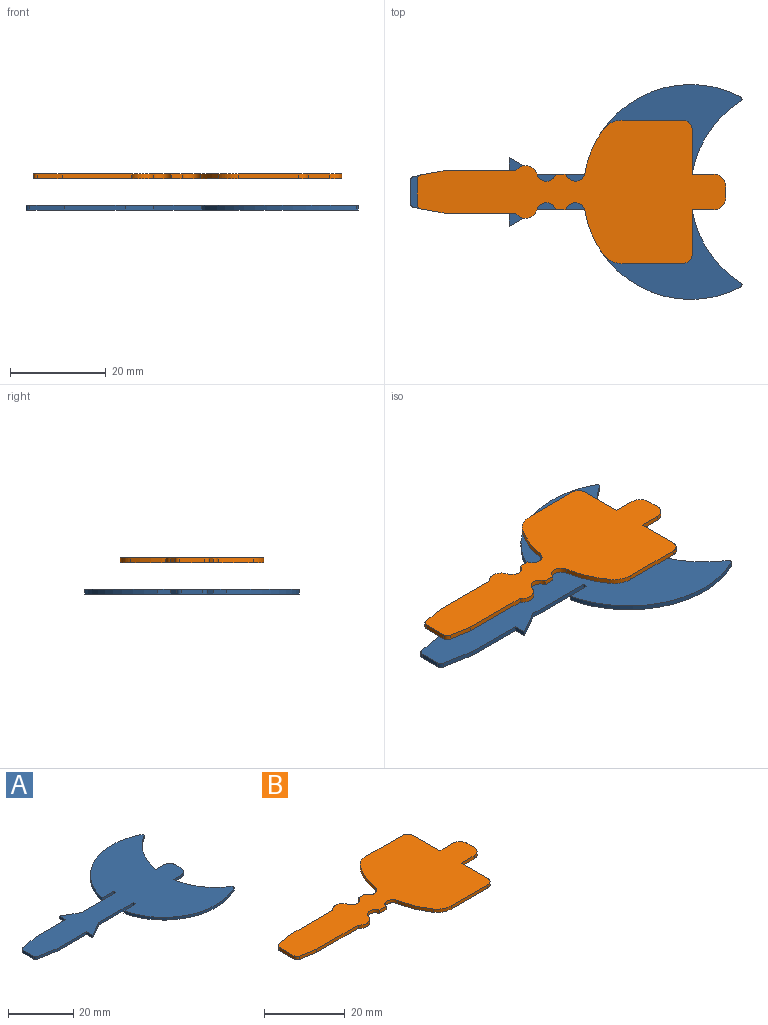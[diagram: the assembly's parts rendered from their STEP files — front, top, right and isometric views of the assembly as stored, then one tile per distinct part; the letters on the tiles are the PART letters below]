
ASSEMBLY  parts=2 mates=1
PART A: 30 faces, bbox 69.5x45x1 mm
  f0: plane 2.5x1mm, normal (1,0,0), area 2.5mm2, adj f12,f13,f14,f27
  f1: plane 3.5x1mm, normal (0,1,0), area 3.5mm2, adj f2,f12,f13,f14
  f2: cylinder r=22.5mm len=15.29mm, axis (0,0,-1), area 18.9mm2, adj f1,f12,f13,f15
  f3: cylinder r=22.5mm len=32.48mm, axis (0,0,-1), area 41.5mm2, adj f4,f12,f13,f15
  f4: plane 5x1mm, normal (0,-1,0), area 5mm2, adj f3,f5,f12,f13
  f5: plane 1x1mm, normal (-1,0,0), area 1mm2, adj f4,f6,f12,f13
  f6: plane 15x1mm, normal (0,1,0), area 15mm2, adj f5,f7,f12,f13
  f7: plane 6x3.46mm, normal (0.5,0.87,0), area 6.9mm2, adj f6,f8,f12,f13
  f8: plane 2.71x1mm, normal (-1,0,0), area 2.7mm2, adj f7,f9,f12,f13
  f9: plane 12.76x1mm, normal (0,1,0), area 12.8mm2, adj f8,f10,f12,f13
  f10: plane 7.17x1.27mm, normal (-0.17,0.98,0), area 7.3mm2, adj f9,f12,f13,f16
  f11: plane 4.5x1mm, normal (-1,0,0), area 4.5mm2, adj f12,f13,f16,f29
  f12: plane 69.5x45mm, normal (0,0,1), area 1314.9mm2, adj f0,f1,f2,f3,f4,f5,f6,f7
  f13: plane 69.5x45mm, normal (0,0,-1), area 1314.9mm2, adj f0,f1,f2,f3,f4,f5,f6,f7
  f14: cylinder r=2.5mm len=2.5mm, axis (0,0,1), area 3.9mm2, adj f0,f1,f12,f13
  f15: cylinder r=0.5mm len=1mm, axis (0,0,1), area 1mm2, adj f2,f3,f12,f13
  f16: cylinder r=1mm len=1mm, axis (0,0,-1), area 1.4mm2, adj f10,f11,f12,f13
  f17: plane 3.5x1mm, normal (0,-1,0), area 3.5mm2, adj f12,f13,f18,f27
  f18: cylinder r=22.5mm len=15.29mm, axis (0,0,-1), area 18.9mm2, adj f12,f13,f17,f28
  f19: cylinder r=22.5mm len=32.48mm, axis (0,0,-1), area 41.5mm2, adj f12,f13,f20,f28
  f20: plane 5x1mm, normal (0,1,0), area 5mm2, adj f12,f13,f19,f21
  f21: plane 1x1mm, normal (-1,0,0), area 1mm2, adj f12,f13,f20,f22
  f22: plane 15x1mm, normal (0,-1,0), area 15mm2, adj f12,f13,f21,f23
  f23: plane 6x3.46mm, normal (0.5,-0.87,0), area 6.9mm2, adj f12,f13,f22,f24
  f24: plane 2.71x1mm, normal (-1,0,0), area 2.7mm2, adj f12,f13,f23,f25
  f25: plane 12.76x1mm, normal (0,-1,0), area 12.8mm2, adj f12,f13,f24,f26
  f26: plane 7.17x1.27mm, normal (-0.17,-0.98,0), area 7.3mm2, adj f12,f13,f25,f29
  f27: cylinder r=2.5mm len=2.5mm, axis (0,0,1), area 3.9mm2, adj f0,f12,f13,f17
  f28: cylinder r=0.5mm len=1mm, axis (0,0,1), area 1mm2, adj f12,f13,f18,f19
  f29: cylinder r=1mm len=1mm, axis (0,0,-1), area 1.4mm2, adj f11,f12,f13,f26
PART B: 32 faces, bbox 64.5x30x1 mm
  f0: plane 2.5x1mm, normal (1,0,0), area 2.5mm2, adj f10,f11,f12,f26
  f1: plane 4.5x1mm, normal (0,1,0), area 4.5mm2, adj f10,f11,f12,f15
  f2: cylinder r=22.5mm len=8.95mm, axis (0,0,-1), area 9.8mm2, adj f3,f10,f11,f16
  f3: cylinder r=2mm len=3.91mm, axis (0,0,-1), area 5.4mm2, adj f2,f4,f10,f11
  f4: plane 2.24x1mm, normal (0,1,0), area 2.2mm2, adj f3,f5,f10,f11
  f5: cylinder r=2mm len=3.86mm, axis (0,0,-1), area 5.2mm2, adj f4,f6,f10,f11
  f6: cylinder r=2.5mm len=4.4mm, axis (0,0,-1), area 5.5mm2, adj f5,f7,f10,f11
  f7: plane 14.63x1mm, normal (0,1,0), area 14.6mm2, adj f6,f8,f10,f11
  f8: plane 5.17x1mm, normal (-0.17,0.98,0), area 5.3mm2, adj f7,f10,f11,f13
  f9: plane 5.21x1mm, normal (-1,0,0), area 5.2mm2, adj f10,f11,f13,f27
  f10: plane 64.5x30mm, normal (0,0,1), area 956.7mm2, adj f0,f1,f2,f3,f4,f5,f6,f7
  f11: plane 64.5x30mm, normal (0,0,-1), area 956.7mm2, adj f0,f1,f2,f3,f4,f5,f6,f7
  f12: cylinder r=2.5mm len=2.5mm, axis (0,0,1), area 3.9mm2, adj f0,f1,f10,f11
  f13: cylinder r=1mm len=1mm, axis (0,0,-1), area 1.4mm2, adj f8,f9,f10,f11
  f14: plane 12.68x1mm, normal (0,1,0), area 12.7mm2, adj f10,f11,f16,f17
  f15: plane 9.25x1mm, normal (1,0,0), area 9.2mm2, adj f1,f10,f11,f17
  f16: cylinder r=5mm len=4.1mm, axis (0,0,-1), area 4.8mm2, adj f2,f10,f11,f14
  f17: cylinder r=2mm len=2mm, axis (0,0,-1), area 3.1mm2, adj f10,f11,f14,f15
  f18: plane 4.5x1mm, normal (0,-1,0), area 4.5mm2, adj f10,f11,f26,f29
  f19: cylinder r=22.5mm len=8.95mm, axis (0,0,-1), area 9.8mm2, adj f10,f11,f20,f30
  f20: cylinder r=2mm len=3.91mm, axis (0,0,-1), area 5.4mm2, adj f10,f11,f19,f21
  f21: plane 2.24x1mm, normal (0,-1,0), area 2.2mm2, adj f10,f11,f20,f22
  f22: cylinder r=2mm len=3.86mm, axis (0,0,-1), area 5.2mm2, adj f10,f11,f21,f23
  f23: cylinder r=2.5mm len=4.4mm, axis (0,0,-1), area 5.5mm2, adj f10,f11,f22,f24
  f24: plane 14.63x1mm, normal (0,-1,0), area 14.6mm2, adj f10,f11,f23,f25
  f25: plane 5.17x1mm, normal (-0.17,-0.98,0), area 5.3mm2, adj f10,f11,f24,f27
  f26: cylinder r=2.5mm len=2.5mm, axis (0,0,1), area 3.9mm2, adj f0,f10,f11,f18
  f27: cylinder r=1mm len=1mm, axis (0,0,-1), area 1.4mm2, adj f9,f10,f11,f25
  f28: plane 12.68x1mm, normal (0,-1,0), area 12.7mm2, adj f10,f11,f30,f31
  f29: plane 9.25x1mm, normal (1,0,0), area 9.2mm2, adj f10,f11,f18,f31
  f30: cylinder r=5mm len=4.1mm, axis (0,0,-1), area 4.8mm2, adj f10,f11,f19,f28
  f31: cylinder r=2mm len=2mm, axis (0,0,-1), area 3.1mm2, adj f10,f11,f28,f29
PLACE A t=(14.7,0,-1)mm
PLACE B t=(14.7,0,5.54)mm
MATE slider B.f2 <-> A.f3  axis (0,0,-1) through (14.7,0,6.04)mm
